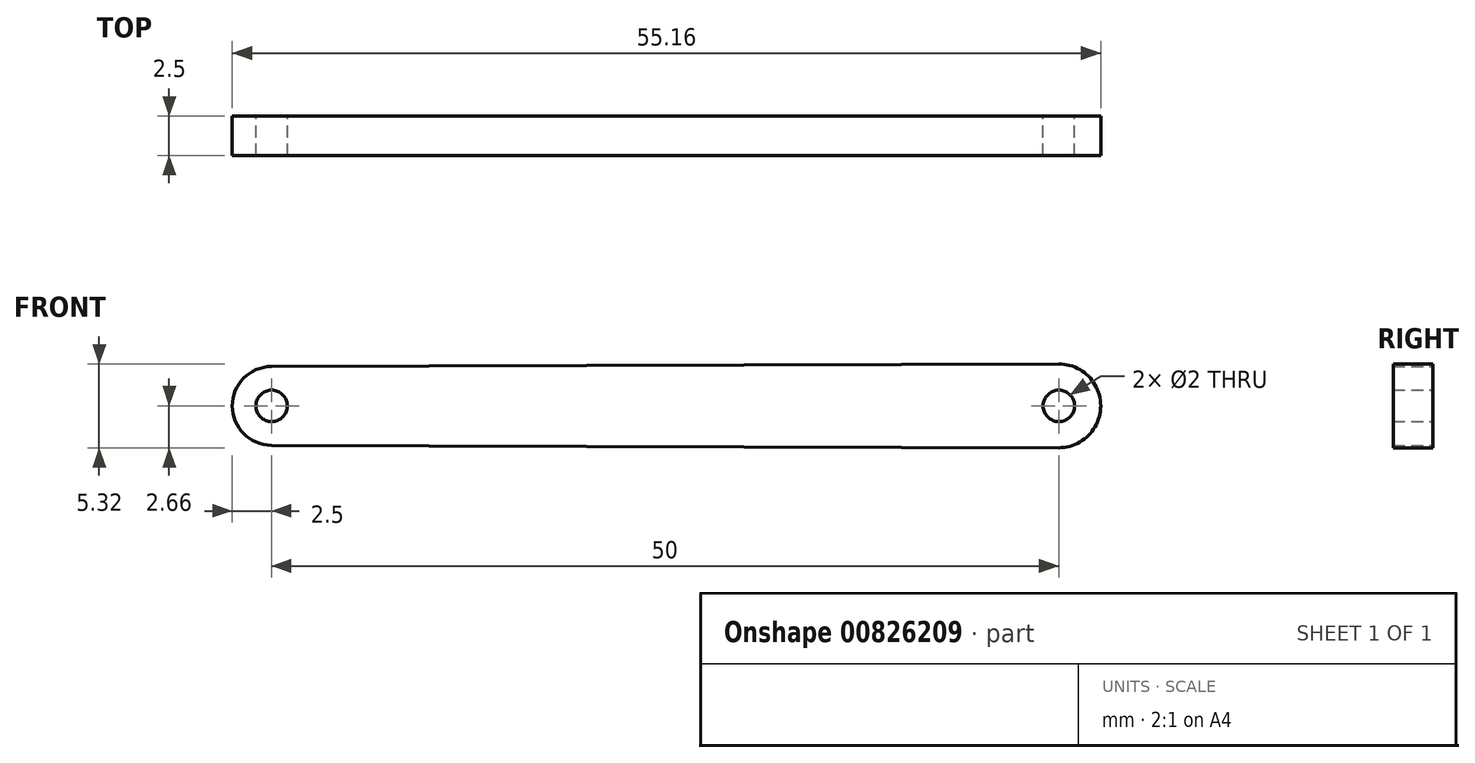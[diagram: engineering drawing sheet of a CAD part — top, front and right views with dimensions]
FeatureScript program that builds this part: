
annotation { "Feature Type Name" : "Feature", "Feature Type Description" : "" }
export const myFeature = defineFeature(function(context is Context, id is Id, definition is map)
    precondition{}
    {
        {
            var Q0;
            Q0=qCreatedBy(makeId("Front.planeOp"),FACE);
            var sketch = newSketch(context, id + "F0", { "sketchPlane" : qUnion([Q0])});
            skCircle(sketch, "E0", {"center": v(0, 0) * mm, "radius": 2.5 * mm});
            skCircle(sketch, "E1", {"center": v(50, 0) * mm, "radius": 2.66 * mm});
            skLineSegment(sketch, "E2", {"start": v(0, 2.5) * mm, "end": v(50, 2.66) * mm});
            skLineSegment(sketch, "E3", {"start": v(0, -2.5) * mm, "end": v(50, -2.66) * mm});
            skCircle(sketch, "E4", {"center": v(0, 0) * mm, "radius": 1 * mm});
            skCircle(sketch, "E5", {"center": v(50, 0) * mm, "radius": 1 * mm});
            skSolve(sketch);
        }
        {
            var Q0;
            Q0 = qSketchRegion(id + "F0", true);
            extrude(context, id + "F1", {"entities" : qUnion([Q0]), "depth" : 2.5 * mm, "offsetDistance" : 25 * mm});
        }
    });
